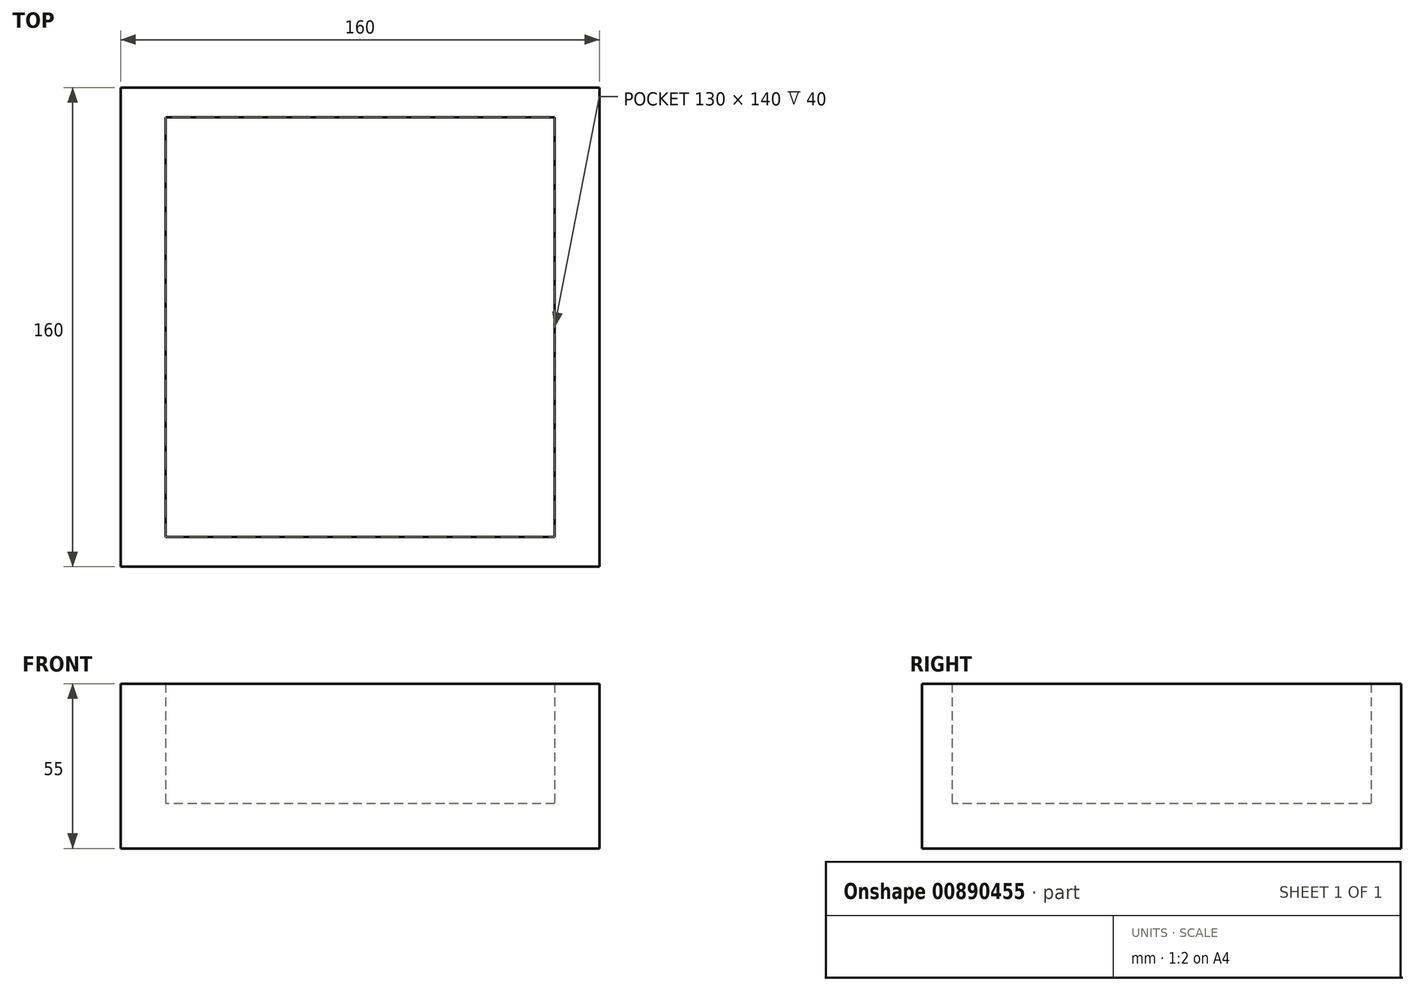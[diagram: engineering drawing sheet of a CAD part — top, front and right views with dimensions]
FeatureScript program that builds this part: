
annotation { "Feature Type Name" : "Feature", "Feature Type Description" : "" }
export const myFeature = defineFeature(function(context is Context, id is Id, definition is map)
    precondition{}
    {
        {
            var Q0;
            Q0=qCreatedBy(makeId("Top.planeOp"),FACE);
            var sketch = newSketch(context, id + "F0", { "sketchPlane" : qUnion([Q0])});
            skLineSegment(sketch, "E0.bottom", {"start": v(80, 80) * mm, "end": v(-80, 80) * mm});
            skLineSegment(sketch, "E0.top", {"start": v(80, -80) * mm, "end": v(-80, -80) * mm});
            skLineSegment(sketch, "E0.left", {"start": v(80, 80) * mm, "end": v(80, -80) * mm});
            skLineSegment(sketch, "E0.right", {"start": v(-80, 80) * mm, "end": v(-80, -80) * mm});
            skPoint(sketch, "E0.middle", {"position": v(0, 0) * mm});
            skLineSegment(sketch, "E1.bottom", {"start": v(65, 70) * mm, "end": v(-65, 70) * mm});
            skLineSegment(sketch, "E1.top", {"start": v(65, -70) * mm, "end": v(-65, -70) * mm});
            skLineSegment(sketch, "E1.left", {"start": v(65, 70) * mm, "end": v(65, -70) * mm});
            skLineSegment(sketch, "E1.right", {"start": v(-65, 70) * mm, "end": v(-65, -70) * mm});
            skSolve(sketch);
        }
        {
            var Q0;
            Q0 = qSketchRegion(id + "F0", true);
            extrude(context, id + "F1", {"entities" : qUnion([Q0]), "depth" : 40 * mm, "offsetDistance" : 25 * mm});
        }
        {
            var Q0;
            Q0=qCreatedBy(makeId("Top.planeOp"),FACE);
            var sketch = newSketch(context, id + "F2", { "sketchPlane" : qUnion([Q0])});
            skLineSegment(sketch, "E2.bottom", {"start": v(80, 80) * mm, "end": v(-80, 80) * mm});
            skLineSegment(sketch, "E2.top", {"start": v(80, -80) * mm, "end": v(-80, -80) * mm});
            skLineSegment(sketch, "E2.left", {"start": v(80, 80) * mm, "end": v(80, -80) * mm});
            skLineSegment(sketch, "E2.right", {"start": v(-80, 80) * mm, "end": v(-80, -80) * mm});
            skPoint(sketch, "E2.middle", {"position": v(0, 0) * mm});
            skSolve(sketch);
        }
        {
            var Q0;
            Q0 = qSketchRegion(id + "F2", true);
            extrude(context, id + "F3", {"entities" : qUnion([Q0]), "operationType" : NewBodyOperationType.ADD, "oppositeDirection" : true, "depth" : 15 * mm, "offsetDistance" : 25 * mm});
        }
    });
